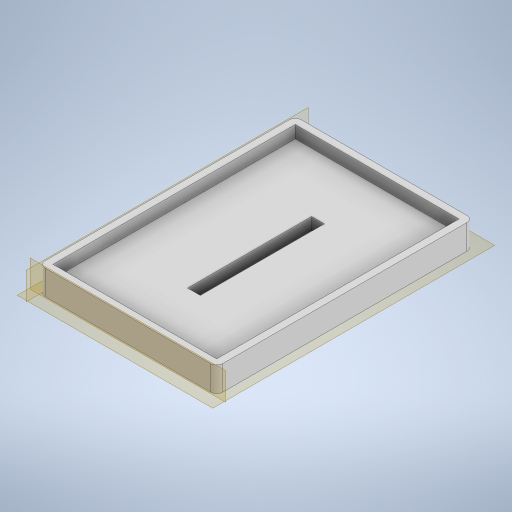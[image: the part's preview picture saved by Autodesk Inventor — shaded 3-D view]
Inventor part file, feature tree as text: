
AUTODESK INVENTOR PART (.ipt)
format: ipt  version: 2024 (Build 280153000, 153)  size: 272,896 bytes
history: native  units: mm
features: extrude x3, sketch x3, fillet x1
ambient origin geometry x8: Origin, YZ Plane, XZ Plane, XY Plane, X Axis, Y Axis, Z Axis, Center Point
bodies: Solid1 (feature_tree)
feature tree (7):
  extrude  "Extrusion1"  Depth=62.0mm
  extrude  "Extrusion2"  TaperAngle=0.0deg  [1 undecoded]
  extrude  "Extrusion3"  Depth=3.0mm
  fillet  "Fillet1"  [1 undecoded]
  sketch  "Sketch1"  dims[d0=43.0mm d1=62.0mm]
  sketch  "Sketch2"  dims[d2=3.0mm d3=0.0mm]
  sketch  "Sketch3"  dims[d4=1.7mm d5=3.0mm d6=0.0mm d7=3.1mm d8=0.0mm d9=30.0mm d11=3.0mm d12=0.0mm d13=1.5mm d15=0.0mm]
note: 2 required parameter values undecoded (feature->parameter linkage not recoverable at this tier; creation-order binding heuristic only, values carry confidence <= 0.55)
